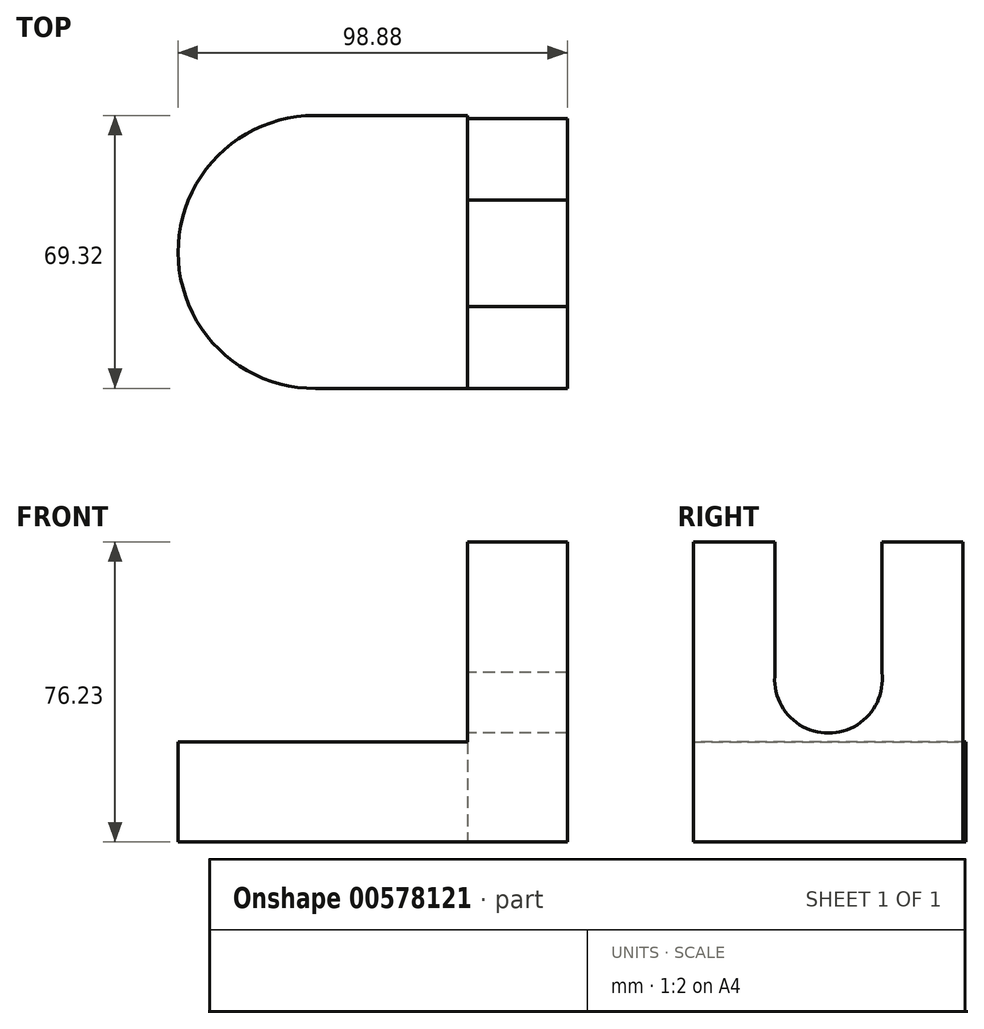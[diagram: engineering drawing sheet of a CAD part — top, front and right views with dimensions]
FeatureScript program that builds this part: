
annotation { "Feature Type Name" : "Feature", "Feature Type Description" : "" }
export const myFeature = defineFeature(function(context is Context, id is Id, definition is map)
    precondition{}
    {
        {
            var Q0;
            Q0=qCreatedBy(makeId("Right.planeOp"),FACE);
            var sketch = newSketch(context, id + "F0", { "sketchPlane" : qUnion([Q0])});
            skLineSegment(sketch, "E0.bottom", {"start": v(-34.66, 76.23) * mm, "end": v(-13.87, 76.23) * mm});
            skLineSegment(sketch, "E0.top", {"start": v(-34.66, 0) * mm, "end": v(33.83, 0) * mm});
            skLineSegment(sketch, "E0.left", {"start": v(-34.66, 76.23) * mm, "end": v(-34.66, 0) * mm});
            skLineSegment(sketch, "E0.right", {"start": v(33.83, 76.23) * mm, "end": v(33.83, 0) * mm});
            skLineSegment(sketch, "E1.left", {"start": v(-13.87, 76.23) * mm, "end": v(-13.87, 41.31) * mm});
            skLineSegment(sketch, "E1.right", {"start": v(13.25, 76.23) * mm, "end": v(13.25, 41.31) * mm});
            skArc(sketch, "E2", {"start": v(-13.87, 43.05) * mm, "mid": v(-0.31, 27.64) * mm, "end": v(13.25, 43.05) * mm});
            skLineSegment(sketch, "E3.trimOffspring", {"start": v(13.25, 76.23) * mm, "end": v(33.83, 76.23) * mm});
            skSolve(sketch);
        }
        {
            var Q0;
            Q0 = qSketchRegion(id + "F0", true);
            extrude(context, id + "F1", {"entities" : qUnion([Q0]), "depth" : 25.4 * mm, "offsetDistance" : 25.4 * mm});
        }
        {
            var Q0;
            Q0=qCreatedBy(makeId("Top.planeOp"),FACE);
            var sketch = newSketch(context, id + "F2", { "sketchPlane" : qUnion([Q0])});
            skLineSegment(sketch, "E4", {"start": v(0, 34.66) * mm, "end": v(-38.82, 34.66) * mm});
            skLineSegment(sketch, "E5", {"start": v(-39.12, -34.66) * mm, "end": v(0, -34.66) * mm});
            skLineSegment(sketch, "E6", {"start": v(0, -34.66) * mm, "end": v(0, 34.66) * mm});
            skArc(sketch, "E7", {"start": v(-38.82, 34.66) * mm, "mid": v(-73.48, -0.15) * mm, "end": v(-38.52, -34.66) * mm});
            skSolve(sketch);
        }
        {
            var Q0;
            Q0 = qSketchRegion(id + "F2", true);
            extrude(context, id + "F3", {"entities" : qUnion([Q0]), "operationType" : NewBodyOperationType.ADD, "depth" : 25.4 * mm, "offsetDistance" : 25.4 * mm});
        }
    });
